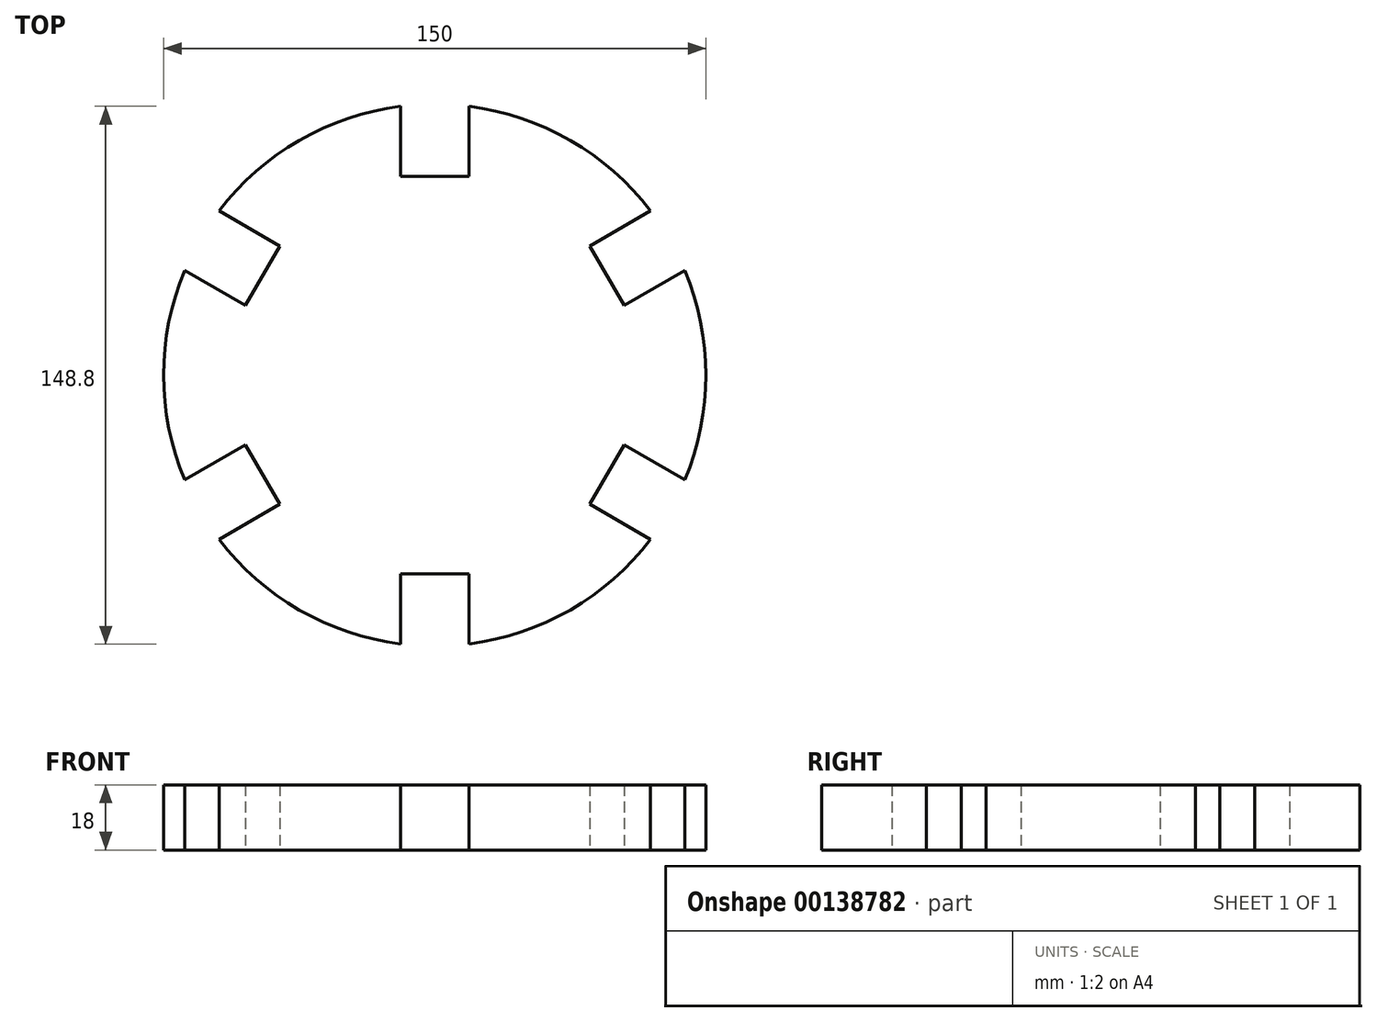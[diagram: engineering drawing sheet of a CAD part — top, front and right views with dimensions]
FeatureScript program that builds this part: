
annotation { "Feature Type Name" : "Feature", "Feature Type Description" : "" }
export const myFeature = defineFeature(function(context is Context, id is Id, definition is map)
    precondition{}
    {
        {
            var Q0;
            Q0=qCreatedBy(makeId("Top.planeOp"),FACE);
            var sketch = newSketch(context, id + "F0", { "sketchPlane" : qUnion([Q0])});
            skCircle(sketch, "E0.cCircle", {"center": v(0, 0) * mm, "radius": 25 * mm, "construction": true});
            skLineSegment(sketch, "E0.0", {"start": v(-18.16, 25) * mm, "end": v(18.16, 25) * mm, "construction": true});
            skLineSegment(sketch, "E0.1", {"start": v(18.16, 25) * mm, "end": v(29.39, -9.55) * mm, "construction": true});
            skLineSegment(sketch, "E0.2", {"start": v(29.39, -9.55) * mm, "end": v(0, -30.9) * mm, "construction": true});
            skLineSegment(sketch, "E0.3", {"start": v(0, -30.9) * mm, "end": v(-29.39, -9.55) * mm, "construction": true});
            skLineSegment(sketch, "E0.4", {"start": v(-29.39, -9.55) * mm, "end": v(-18.16, 25) * mm, "construction": true});
            skPoint(sketch, "E0.0.midPoint", {"position": v(0, 25) * mm});
            skCircle(sketch, "E1.cCircle", {"center": v(0, 0) * mm, "radius": 55 * mm, "construction": true});
            skLineSegment(sketch, "E1.0", {"start": v(-39.96, 55) * mm, "end": v(39.96, 55) * mm, "construction": true});
            skLineSegment(sketch, "E1.1", {"start": v(39.96, 55) * mm, "end": v(64.66, -21) * mm, "construction": true});
            skLineSegment(sketch, "E1.2", {"start": v(64.66, -21) * mm, "end": v(0, -67.98) * mm, "construction": true});
            skLineSegment(sketch, "E1.3", {"start": v(0, -67.98) * mm, "end": v(-64.66, -21) * mm, "construction": true});
            skLineSegment(sketch, "E1.4", {"start": v(-64.66, -21) * mm, "end": v(-39.96, 55) * mm, "construction": true});
            skPoint(sketch, "E1.0.midPoint", {"position": v(0, 55) * mm});
            skArc(sketch, "E2", {"start": v(-9.5, 74.4) * mm, "mid": v(-37.5, 64.95) * mm, "end": v(-59.68, 45.43) * mm});
            skLineSegment(sketch, "E3.bottom", {"start": v(-9.5, 55) * mm, "end": v(9.5, 55) * mm});
            skLineSegment(sketch, "E3.left", {"start": v(-9.5, 55) * mm, "end": v(-9.5, 74.4) * mm});
            skLineSegment(sketch, "E3.right", {"start": v(9.5, 55) * mm, "end": v(9.5, 74.4) * mm});
            skLineSegment(sketch, "E4.1.0", {"start": v(-42.88, 35.73) * mm, "end": v(-59.68, 45.43) * mm});
            skLineSegment(sketch, "E4.1.1", {"start": v(-52.38, 19.27) * mm, "end": v(-42.88, 35.73) * mm});
            skPoint(sketch, "E4.1.2", {"position": v(-47.63, 27.5) * mm});
            skLineSegment(sketch, "E4.1.3", {"start": v(-52.38, 19.27) * mm, "end": v(-69.18, 28.97) * mm});
            skLineSegment(sketch, "E4.2.0", {"start": v(-52.38, -19.27) * mm, "end": v(-69.18, -28.97) * mm});
            skLineSegment(sketch, "E4.2.1", {"start": v(-42.88, -35.73) * mm, "end": v(-52.38, -19.27) * mm});
            skPoint(sketch, "E4.2.2", {"position": v(-47.63, -27.5) * mm});
            skLineSegment(sketch, "E4.2.3", {"start": v(-42.88, -35.73) * mm, "end": v(-59.68, -45.43) * mm});
            skLineSegment(sketch, "E4.3.0", {"start": v(-9.5, -55) * mm, "end": v(-9.5, -74.4) * mm});
            skLineSegment(sketch, "E4.3.1", {"start": v(9.5, -55) * mm, "end": v(-9.5, -55) * mm});
            skPoint(sketch, "E4.3.2", {"position": v(0, -55) * mm});
            skLineSegment(sketch, "E4.3.3", {"start": v(9.5, -55) * mm, "end": v(9.5, -74.4) * mm});
            skLineSegment(sketch, "E4.4.0", {"start": v(42.88, -35.73) * mm, "end": v(59.68, -45.43) * mm});
            skLineSegment(sketch, "E4.4.1", {"start": v(52.38, -19.27) * mm, "end": v(42.88, -35.73) * mm});
            skPoint(sketch, "E4.4.2", {"position": v(47.63, -27.5) * mm});
            skLineSegment(sketch, "E4.4.3", {"start": v(52.38, -19.27) * mm, "end": v(69.18, -28.97) * mm});
            skArc(sketch, "E5.trimOffspring", {"start": v(-69.18, 28.97) * mm, "mid": v(-75, 0) * mm, "end": v(-69.18, -28.97) * mm});
            skArc(sketch, "E6.trimOffspring", {"start": v(59.68, 45.43) * mm, "mid": v(37.5, 64.95) * mm, "end": v(9.5, 74.4) * mm});
            skArc(sketch, "E7.trimOffspring", {"start": v(9.5, -74.4) * mm, "mid": v(37.5, -64.95) * mm, "end": v(59.68, -45.43) * mm});
            skArc(sketch, "E8.trimOffspring", {"start": v(-59.68, -45.43) * mm, "mid": v(-37.5, -64.95) * mm, "end": v(-9.5, -74.4) * mm});
            skLineSegment(sketch, "E9.3.5.0", {"start": v(42.88, 35.73) * mm, "end": v(52.38, 19.27) * mm});
            skLineSegment(sketch, "E9.4.5.0", {"start": v(52.38, 19.27) * mm, "end": v(69.18, 28.97) * mm});
            skPoint(sketch, "E9.6.5.0", {"position": v(47.63, 27.5) * mm});
            skLineSegment(sketch, "E9.7.5.0", {"start": v(42.88, 35.73) * mm, "end": v(59.68, 45.43) * mm});
            skArc(sketch, "E10.trimOffspring", {"start": v(69.18, -28.97) * mm, "mid": v(75, 0) * mm, "end": v(69.18, 28.97) * mm});
            skSolve(sketch);
        }
        {
            var Q0;
            Q0=qSketchRegion(id+"F0",true);
            extrude(context, id + "F1", {"entities" : qUnion([Q0]), "depth" : 18 * mm});
        }
    });
